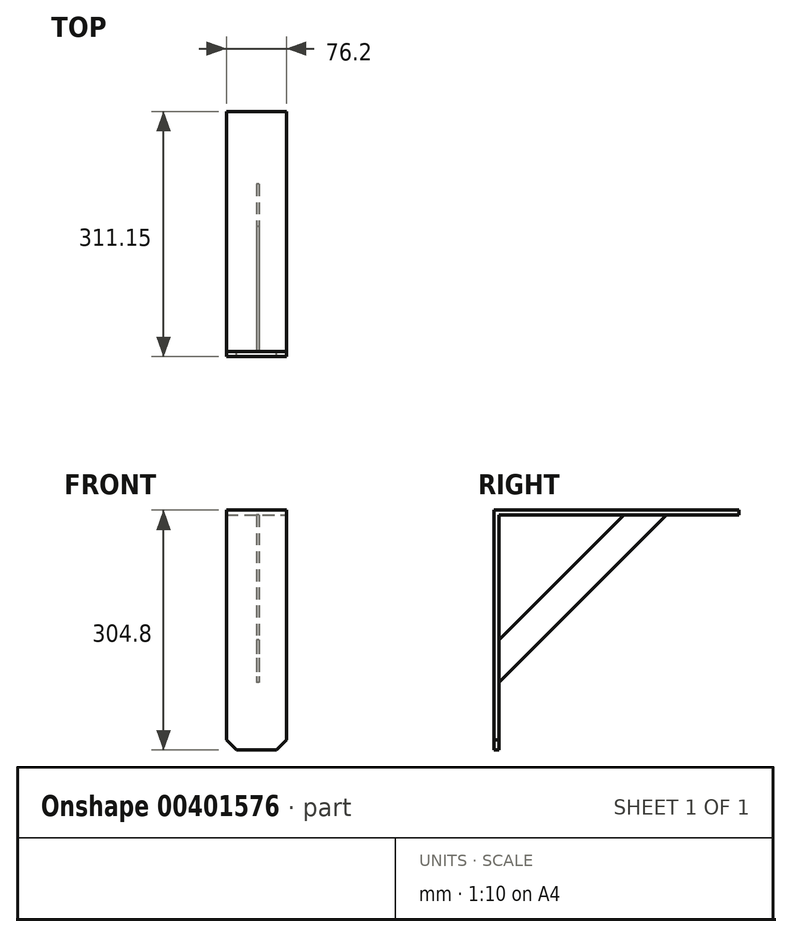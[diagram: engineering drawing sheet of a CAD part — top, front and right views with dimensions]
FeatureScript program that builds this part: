
annotation { "Feature Type Name" : "Feature", "Feature Type Description" : "" }
export const myFeature = defineFeature(function(context is Context, id is Id, definition is map)
    precondition{}
    {
        {
            var Q0;
            Q0=qCreatedBy(makeId("Front.planeOp"),FACE);
            var sketch = newSketch(context, id + "F0", { "sketchPlane" : qUnion([Q0])});
            skLineSegment(sketch, "E0.bottom", {"start": v(25.4, -152.4) * mm, "end": v(-38.1, -152.4) * mm});
            skLineSegment(sketch, "E0.top", {"start": v(38.1, 152.4) * mm, "end": v(-38.1, 152.4) * mm});
            skLineSegment(sketch, "E0.left", {"start": v(38.1, -139.7) * mm, "end": v(38.1, 152.4) * mm});
            skLineSegment(sketch, "E0.right", {"start": v(-38.1, -139.7) * mm, "end": v(-38.1, 152.4) * mm});
            skPoint(sketch, "E0.middle", {"position": v(0, 0) * mm});
            skLineSegment(sketch, "E1", {"start": v(-38.1, -139.7) * mm, "end": v(-25.4, -152.4) * mm});
            skLineSegment(sketch, "E2", {"start": v(25.4, -152.4) * mm, "end": v(38.1, -139.7) * mm});
            skPoint(sketch, "E3.orphan", {"position": v(38.1, -152.4) * mm});
            skSolve(sketch);
        }
        {
            var Q0;
            Q0=makeQuery(id+"F0.imprint","IMPRINT",FACE,{"disambiguationData":[TD([[makeQuery(id+"F0.imprint","IMPRINT",EDGE,{"derivedFrom":sQuery(id+"F0.wireOp",EDGE,"E0.bottom")}),-1.0]])]});
            extrude(context, id + "F1", {"entities" : qUnion([Q0]), "depth" : 6.35 * mm});
        }
        {
            var Q0;
            Q0=qCreatedBy(makeId("Right.planeOp"),FACE);
            cPlane(context, id + "F2", {"entities" : qUnion([Q0]), "cplaneType" : CPlaneType.OFFSET, "offset" : 38.1 * mm, "width" : 152.4 * mm, "height" : 152.4 * mm});
        }
        {
            var Q0;
            Q0=qCreatedBy(id+"F2.planeOp",FACE);
            var sketch = newSketch(context, id + "F3", { "sketchPlane" : qUnion([Q0])});
            skLineSegment(sketch, "E4.bottom", {"start": v(0, 152.26) * mm, "end": v(304.8, 152.26) * mm});
            skLineSegment(sketch, "E4.top", {"start": v(0, 145.91) * mm, "end": v(304.8, 145.91) * mm});
            skLineSegment(sketch, "E4.left", {"start": v(0, 152.26) * mm, "end": v(0, 145.91) * mm});
            skLineSegment(sketch, "E4.right", {"start": v(304.8, 152.26) * mm, "end": v(304.8, 145.91) * mm});
            skSolve(sketch);
        }
        {
            var Q0;
            Q0=makeQuery(id+"F3.imprint","IMPRINT",FACE,{"disambiguationData":[TD([[makeQuery(id+"F3.imprint","IMPRINT",EDGE,{"derivedFrom":sQuery(id+"F3.wireOp",EDGE,"E4.bottom")}),-1.0]])]});
            extrude(context, id + "F4", {"entities" : qUnion([Q0]), "operationType" : NewBodyOperationType.ADD, "oppositeDirection" : true, "depth" : 76.2 * mm});
        }
        {
            var Q0;
            Q0=qCreatedBy(makeId("Right.planeOp"),FACE);
            var sketch = newSketch(context, id + "F5", { "sketchPlane" : qUnion([Q0])});
            skLineSegment(sketch, "E5", {"start": v(212.56, 145.91) * mm, "end": v(0, -66.65) * mm});
            skLineSegment(sketch, "E6", {"start": v(158.68, 145.91) * mm, "end": v(0, -12.77) * mm});
            skLineSegment(sketch, "E7", {"start": v(212.56, 145.91) * mm, "end": v(158.68, 145.91) * mm});
            skLineSegment(sketch, "E8", {"start": v(0, -12.77) * mm, "end": v(0, -66.65) * mm});
            skPoint(sketch, "E9", {"position": v(215.9, 145.66) * mm});
            skPoint(sketch, "E10", {"position": v(0, -63.5) * mm});
            skSolve(sketch);
        }
        {
            var Q0;
            Q0=makeQuery(id+"F5.imprint","IMPRINT",FACE,{"disambiguationData":[TD([[makeQuery(id+"F5.imprint","IMPRINT",EDGE,{"derivedFrom":sQuery(id+"F5.wireOp",EDGE,"E5")}),-1.0]])]});
            extrude(context, id + "F6", {"entities" : qUnion([Q0]), "operationType" : NewBodyOperationType.ADD, "depth" : 3.17 * mm});
        }
        {
            var Q0;
            Q0 = qSketchRegion(id + "F5", true);
            extrude(context, id + "F7", {"entities" : qUnion([Q0]), "operationType" : NewBodyOperationType.ADD, "depth" : 3.17 * mm});
        }
    });
